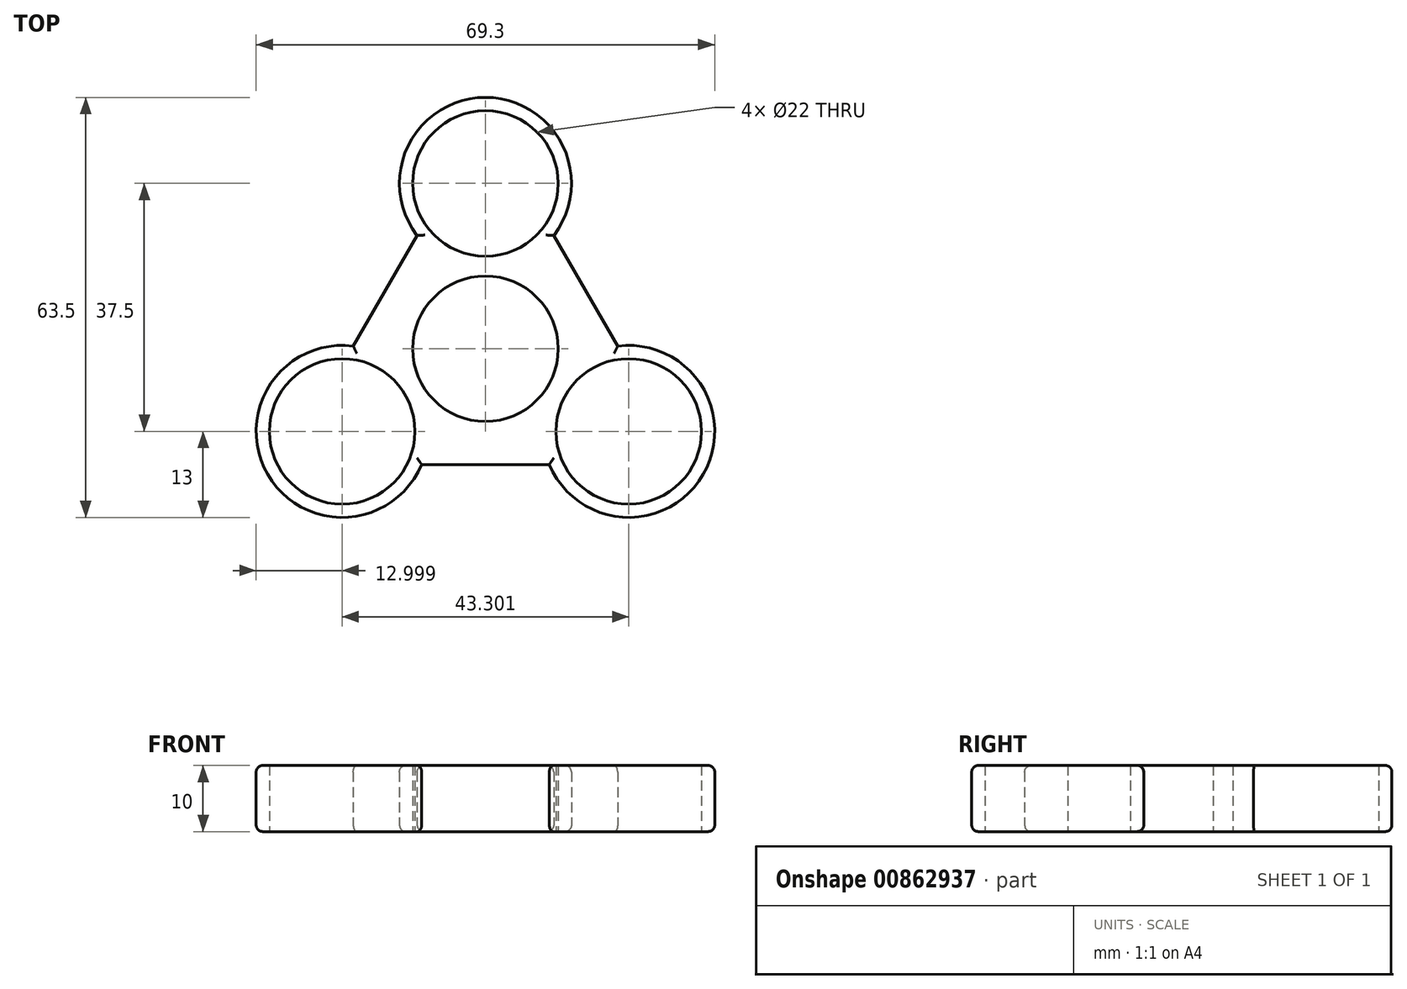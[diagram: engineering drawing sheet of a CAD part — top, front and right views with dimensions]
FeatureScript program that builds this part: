
annotation { "Feature Type Name" : "Feature", "Feature Type Description" : "" }
export const myFeature = defineFeature(function(context is Context, id is Id, definition is map)
    precondition{}
    {
        {
            var Q0;
            Q0=qCreatedBy(makeId("Top.planeOp"),FACE);
            var sketch = newSketch(context, id + "F0", { "sketchPlane" : qUnion([Q0])});
            skPoint(sketch, "E0.0.midPoint", {"position": v(0, -12.5) * mm});
            skCircle(sketch, "E1", {"center": v(0, 0) * mm, "radius": 11 * mm});
            skCircle(sketch, "E2", {"center": v(0, 25) * mm, "radius": 11 * mm});
            skCircle(sketch, "E3", {"center": v(-21.65, -12.5) * mm, "radius": 11 * mm});
            skCircle(sketch, "E4", {"center": v(21.65, -12.5) * mm, "radius": 11 * mm});
            skArc(sketch, "E5", {"start": v(10.33, 17.1) * mm, "mid": v(0, 38) * mm, "end": v(-10.33, 17.1) * mm});
            skArc(sketch, "E6", {"start": v(-19.98, 0.4) * mm, "mid": v(-32.9, -19) * mm, "end": v(-9.65, -17.5) * mm});
            skArc(sketch, "E7", {"start": v(9.65, -17.5) * mm, "mid": v(32.9, -19) * mm, "end": v(19.98, 0.4) * mm});
            skLineSegment(sketch, "E8.0", {"start": v(9.65, -17.5) * mm, "end": v(-9.65, -17.5) * mm});
            skLineSegment(sketch, "E8.1", {"start": v(-19.98, 0.4) * mm, "end": v(-10.33, 17.1) * mm});
            skLineSegment(sketch, "E8.2", {"start": v(10.33, 17.1) * mm, "end": v(19.98, 0.4) * mm});
            skPoint(sketch, "E8.0.midPoint", {"position": v(0, -17.5) * mm});
            skSolve(sketch);
        }
        {
            var Q0;
            Q0=makeQuery(id+"F0.imprint","IMPRINT",FACE,{"disambiguationData":[TD([[makeQuery(id+"F0.imprint","IMPRINT",EDGE,{"derivedFrom":sQuery(id+"F0.wireOp",EDGE,"E1")}),-1.0]])]});
            extrude(context, id + "F1", {"entities" : qUnion([Q0]), "depth" : 10 * mm, "offsetDistance" : 25 * mm});
        }
        {
            var Q0;
            Q0=makeQuery(id+"F1.opExtrude","CAP_EDGE",EDGE,{"disambiguationData":[OSD([sQuery(id+"F0.wireOp",EDGE,"E6")])],"isStart":false});
            var Q1;
            Q1=makeQuery(id+"F1.opExtrude","CAP_EDGE",EDGE,{"disambiguationData":[OSD([sQuery(id+"F0.wireOp",EDGE,"E8.0")])],"isStart":false});
            var Q2;
            Q2=makeQuery(id+"F1.opExtrude","CAP_EDGE",EDGE,{"disambiguationData":[OSD([sQuery(id+"F0.wireOp",EDGE,"E7")])],"isStart":false});
            var Q3;
            Q3=makeQuery(id+"F1.opExtrude","CAP_EDGE",EDGE,{"disambiguationData":[OSD([sQuery(id+"F0.wireOp",EDGE,"E8.2")])],"isStart":false});
            var Q4;
            Q4=makeQuery(id+"F1.opExtrude","CAP_EDGE",EDGE,{"disambiguationData":[OSD([sQuery(id+"F0.wireOp",EDGE,"E5")])],"isStart":false});
            var Q5;
            Q5=makeQuery(id+"F1.opExtrude","CAP_EDGE",EDGE,{"disambiguationData":[OSD([sQuery(id+"F0.wireOp",EDGE,"E8.1")])],"isStart":false});
            var Q6;
            Q6=makeQuery(id+"F1.opExtrude","CAP_EDGE",EDGE,{"disambiguationData":[OSD([sQuery(id+"F0.wireOp",EDGE,"E8.2")])],"isStart":true});
            var Q7;
            Q7=makeQuery(id+"F1.opExtrude","CAP_EDGE",EDGE,{"disambiguationData":[OSD([sQuery(id+"F0.wireOp",EDGE,"E7")])],"isStart":true});
            var Q8;
            Q8=makeQuery(id+"F1.opExtrude","CAP_EDGE",EDGE,{"disambiguationData":[OSD([sQuery(id+"F0.wireOp",EDGE,"E8.0")])],"isStart":true});
            var Q9;
            Q9=makeQuery(id+"F1.opExtrude","CAP_EDGE",EDGE,{"disambiguationData":[OSD([sQuery(id+"F0.wireOp",EDGE,"E6")])],"isStart":true});
            var Q10;
            Q10=makeQuery(id+"F1.opExtrude","CAP_EDGE",EDGE,{"disambiguationData":[OSD([sQuery(id+"F0.wireOp",EDGE,"E8.1")])],"isStart":true});
            var Q11;
            Q11=makeQuery(id+"F1.opExtrude","CAP_EDGE",EDGE,{"disambiguationData":[OSD([sQuery(id+"F0.wireOp",EDGE,"E5")])],"isStart":true});
            fillet(context, id + "F2", {"entities" : qUnion([Q0, Q1, Q2, Q3, Q4, Q5, Q6, Q7, Q8, Q9, Q10, Q11]), "radius" : 1 * mm, "tangentPropagation" : true, "allowEdgeOverflow" : false});
        }
    });
